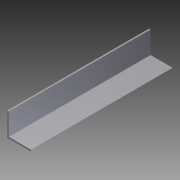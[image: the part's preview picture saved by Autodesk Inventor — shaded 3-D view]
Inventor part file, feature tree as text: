
AUTODESK INVENTOR PART (.ipt)
format: ipt  version: 2012 (Build 160160000, 160)  size: 73,728 bytes
history: native  units: in
note: dims shown in document units (in); Inventor stores cm internally (conversion verified against a paired STEP export)
features: extrude x1, sketch x1
ambient origin geometry x8: Origin, YZ Plane, XZ Plane, XY Plane, X Axis, Y Axis, Z Axis, Center Point
bodies: Solid1 (feature_tree)
feature tree (2):
  extrude  "Extrusion1"  Depth=1.0in
  sketch  "Sketch1"  dims[d0=1.0in d1=1.0in d2=0.0625in d3=0.0625in d4=6.0in d5=0.0in]
